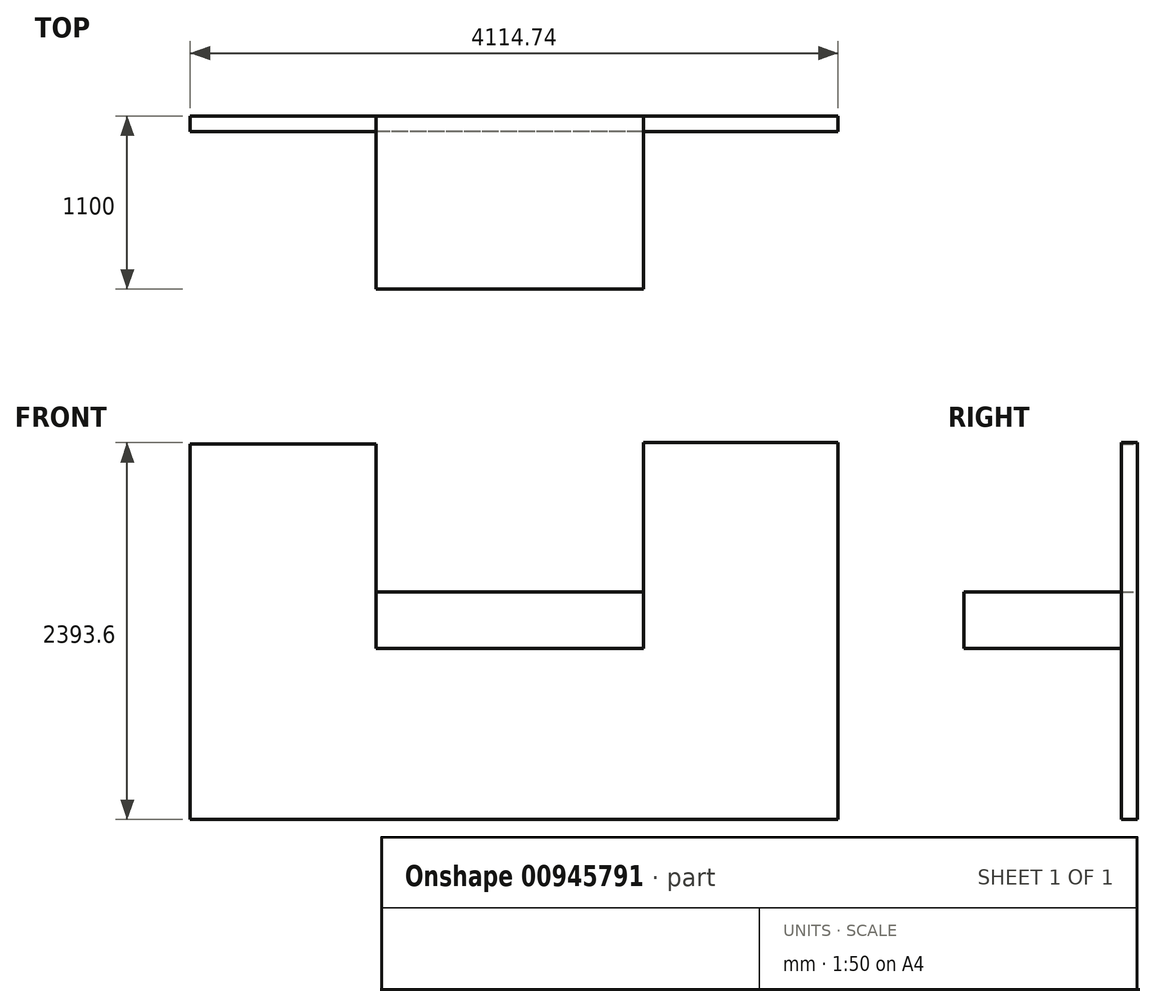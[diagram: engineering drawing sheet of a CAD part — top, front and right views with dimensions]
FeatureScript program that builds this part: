
annotation { "Feature Type Name" : "Feature", "Feature Type Description" : "" }
export const myFeature = defineFeature(function(context is Context, id is Id, definition is map)
    precondition{}
    {
        {
            var Q0;
            Q0=qCreatedBy(makeId("Front.planeOp"),FACE);
            var sketch = newSketch(context, id + "F0", { "sketchPlane" : qUnion([Q0])});
            skLineSegment(sketch, "E0.bottom", {"start": v(-168.5, 277.98) * mm, "end": v(1531.5, 277.98) * mm});
            skLineSegment(sketch, "E0.top", {"start": v(-168.5, -82.02) * mm, "end": v(1531.5, -82.02) * mm});
            skLineSegment(sketch, "E0.left", {"start": v(-168.5, 277.98) * mm, "end": v(-168.5, -82.02) * mm});
            skLineSegment(sketch, "E0.right", {"start": v(1531.5, 277.98) * mm, "end": v(1531.5, -82.02) * mm});
            skSolve(sketch);
        }
        {
            var Q0;
            Q0=makeQuery(id+"F0.imprint","IMPRINT",FACE,{"disambiguationData":[TD([[makeQuery(id+"F0.imprint","IMPRINT",EDGE,{"derivedFrom":sQuery(id+"F0.wireOp",EDGE,"E0.bottom")}),-1.0]])]});
            extrude(context, id + "F1", {"entities" : qUnion([Q0]), "depth" : 1100 * mm, "offsetDistance" : 25 * mm});
        }
        {
            var Q0;
            Q0=makeQuery(id+"F1.opExtrude","CAP_FACE",FACE,{"disambiguationData":[OSD([sQuery(id+"F0.wireOp",EDGE,"E0.bottom"),sQuery(id+"F0.wireOp",EDGE,"E0.top"),sQuery(id+"F0.wireOp",EDGE,"E0.left"),sQuery(id+"F0.wireOp",EDGE,"E0.right")])],"isStart":true});
            var sketch = newSketch(context, id + "F2", { "sketchPlane" : qUnion([Q0])});
            skLineSegment(sketch, "E1.bottom", {"start": v(-1531.5, 277.98) * mm, "end": v(168.5, 277.98) * mm});
            skLineSegment(sketch, "E1.top", {"start": v(-2766.4, -1168.03) * mm, "end": v(1348.35, -1168.03) * mm});
            skLineSegment(sketch, "E1.left", {"start": v(-2766.4, 277.98) * mm, "end": v(-2766.4, -1168.03) * mm});
            skLineSegment(sketch, "E1.right", {"start": v(1348.35, 277.98) * mm, "end": v(1348.35, -1168.03) * mm});
            skLineSegment(sketch, "E2.top", {"start": v(168.5, 1217.56) * mm, "end": v(1348.35, 1217.56) * mm});
            skLineSegment(sketch, "E2.left", {"start": v(168.5, 277.98) * mm, "end": v(168.5, 1217.56) * mm});
            skLineSegment(sketch, "E2.right", {"start": v(1348.35, -82.02) * mm, "end": v(1348.35, 1217.56) * mm});
            skLineSegment(sketch, "E3.top", {"start": v(-1531.5, 1225.57) * mm, "end": v(-2766.4, 1225.57) * mm});
            skLineSegment(sketch, "E3.left", {"start": v(-1531.5, 277.98) * mm, "end": v(-1531.5, 1225.57) * mm});
            skLineSegment(sketch, "E3.right", {"start": v(-2766.4, -82.02) * mm, "end": v(-2766.4, 1225.57) * mm});
            skSolve(sketch);
        }
        {
            var Q0;
            Q0 = qSketchRegion(id + "F2", true);
            extrude(context, id + "F3", {"entities" : qUnion([Q0]), "operationType" : NewBodyOperationType.ADD, "oppositeDirection" : true, "depth" : 100 * mm, "offsetDistance" : 25 * mm});
        }
    });
